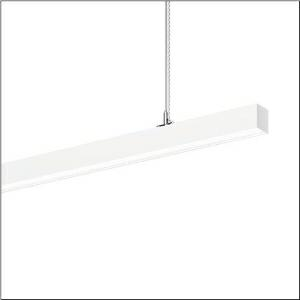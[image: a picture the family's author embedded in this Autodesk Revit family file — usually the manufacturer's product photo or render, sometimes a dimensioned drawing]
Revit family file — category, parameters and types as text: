
# Revit family: silica_21_51mx33tbt9w
name_source: partatom
category: Lighting Fixtures
units: mm (PartAtom-declared; Revit-internal decimal feet)

## family parameters
Cut with Voids When Loaded = No
Host = Face
Light Source = No
Part Type = Normal
Room Calculation Point = No
Round Connector Dimension = Use Diameter
Shared = No

## types (1)
- --- (1 x LED, 7170 lm, 67.4 W, 6500K)
    Apparent Load = 67 VA
    CIE Flux Codes = 78 96 99 56 100
    Color Rendering = 80
    Color Temperature = 6500K
    Default Elevation = 1800 mm
    Description = Silica 21, office luminaire, primary optical cover: prismatic diffuser, of PMMA, CAT 2 (L<= 3000cd/m²), light emission: direct/indirect distribution, primary light characteristic: symmetric, installation type: suspended mounting, LED, rated luminous flux: 7.170lm, luminous efficacy: 101lm/W, light colour: 8tw, colour temperature: 2700..6500K, control gear: DALI DT8, with terminal, 3+2-pole, max. 2.5mm², mains connection: 220..240V, AC, 50/60Hz, rated input power: 70.8W, luminaire housing, of aluminium, traffic white (RAL 9016), length: 1.504mm, width: 53mm, height: 53mm, protection rating (complete): IP20, insulation class (complete): insulation class I (protective earthing), certification: CE, permissible operating ambient temperature: 0..+35°C, standard: EN 50419, packaging unit: 1 piece
    Height = 53 mm
    Lamp = 1 x LED
    Lamp Light Flux = 7170 lm
    Lamp Power = 67.4 W
    Lamp count = 1
    Length = 1504 mm
    Luminous efficacy = 106 lm/W
    Manufacturer = Siteco
    ModVariant = No
    Model = 51MX33TBT9W
    Mounting Place = Ceiling
    Mounting Type = Pendant
    Number of Poles = 1
    OnlyDefault = Yes
    Power Factor = 1
    Product Name = Silica 21
    Product group = office luminaire | ceiling pendant
    ProductGroupID = 903
    Protection Class = Protection class I
    Protection Degree = IP 20
    RLX_Detail_Level = 1
    RLX_Emergency_Light_Flux = 0 lm
    RLX_Emergency_Type = 0
    RLX_Emergency_Type_DB = No
    RlxData = <blob elided: 18197 chars, md5=dc4a4a25>
    Socket = socket
    Standby Power = 0 W
    System Light Flux = 7170 lm
    System Power = 67 W
    Type Comments = individual setting
    Type Image = l_1349007.jpg
    URL = http://relux.com
    VarID = @adj_139271
    Voltage = 0 V
    Weight = 0.00 kg
    Width = 53 mm

## geometry (parser evidence)
native form markers: Blend x4, Sweep x14
no freeform markers — native parametric forms only
